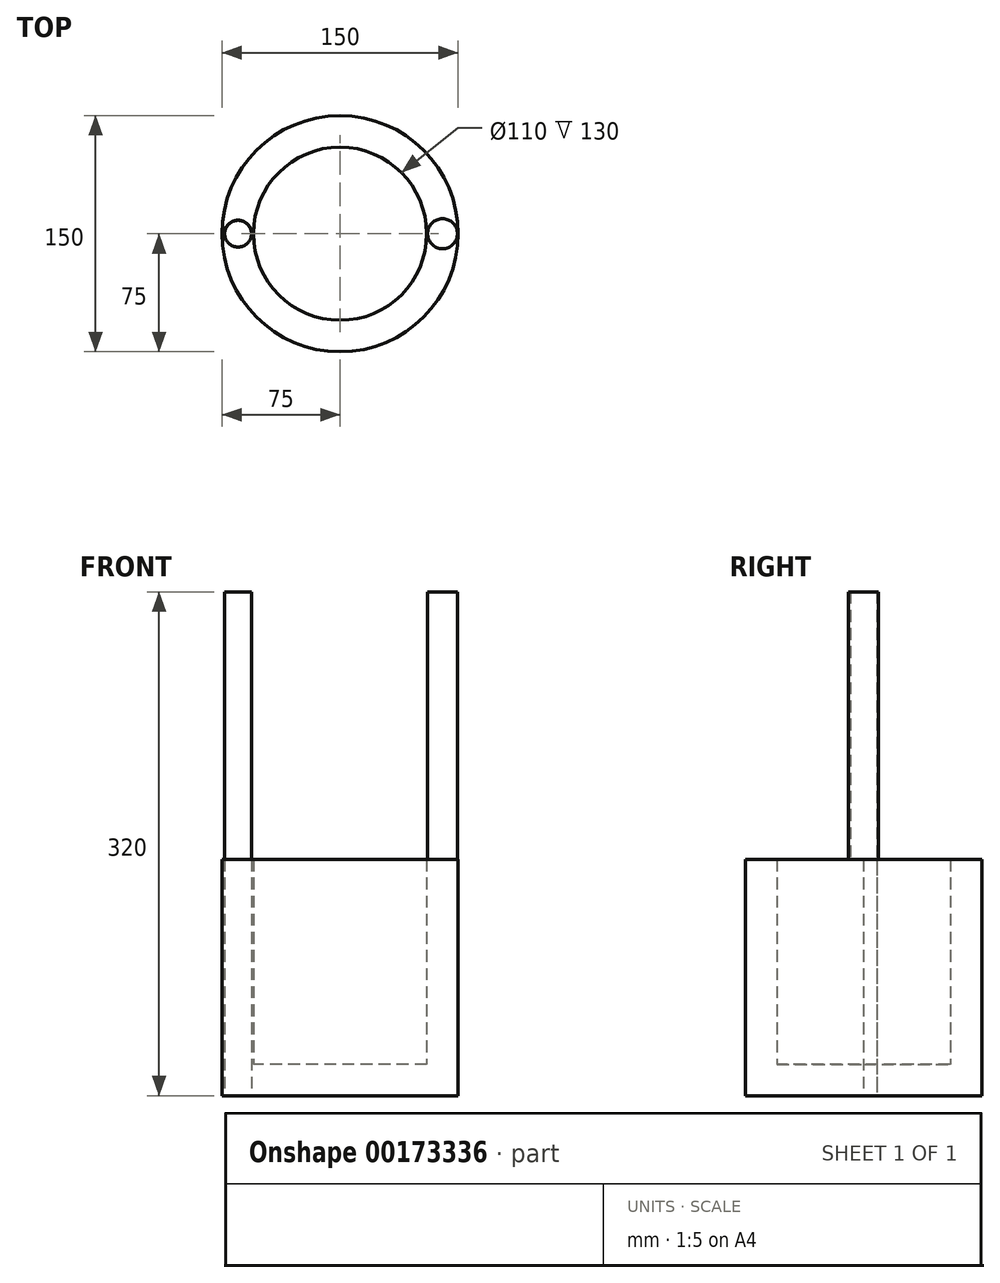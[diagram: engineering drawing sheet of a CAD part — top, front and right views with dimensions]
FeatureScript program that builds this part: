
annotation { "Feature Type Name" : "Feature", "Feature Type Description" : "" }
export const myFeature = defineFeature(function(context is Context, id is Id, definition is map)
    precondition{}
    {
        {
            var Q0;
            Q0=qCreatedBy(makeId("Top.planeOp"),FACE);
            var sketch = newSketch(context, id + "F0", { "sketchPlane" : qUnion([Q0])});
            skCircle(sketch, "E0", {"center": v(0, 0) * mm, "radius": 75 * mm});
            skCircle(sketch, "E1", {"center": v(0, 0) * mm, "radius": 55 * mm});
            skCircle(sketch, "E2", {"center": v(-64.8, 0) * mm, "radius": 8.5 * mm});
            skCircle(sketch, "E3", {"center": v(65.05, 0) * mm, "radius": 9.5 * mm});
            skArc(sketch, "E4", {"start": v(-55, 0) * mm, "mid": v(-65, 10.17) * mm, "end": v(-75, 0) * mm});
            skArc(sketch, "E5", {"start": v(-56.3, 0) * mm, "mid": v(-64.8, 8.57) * mm, "end": v(-73.3, 0) * mm});
            skSolve(sketch);
        }
        {
            var Q0;
            Q0=makeQuery(id+"F0.imprint","IMPRINT",FACE,{"disambiguationData":[TD([[makeQuery(id+"F0.imprint","IMPRINT",EDGE,{"derivedFrom":sQuery(id+"F0.wireOp",EDGE,"E0")}),1.0]])]});
            extrude(context, id + "F1", {"entities" : qUnion([Q0]), "depth" : 150 * mm});
        }
        {
            var Q0;
            Q0=makeQuery(id+"F0.imprint","IMPRINT",FACE,{"disambiguationData":[TD([[makeQuery(id+"F0.imprint","IMPRINT",EDGE,{"derivedFrom":sQuery(id+"F0.wireOp",EDGE,"E0")}),1.0]])]});
            var Q1;
            Q1=makeQuery(id+"F0.imprint","IMPRINT",FACE,{"disambiguationData":[TD([[makeQuery(id+"F0.imprint","IMPRINT",EDGE,{"derivedFrom":sQuery(id+"F0.wireOp",EDGE,"E1")}),1.0]])]});
            extrude(context, id + "F2", {"entities" : qUnion([Q0, Q1]), "operationType" : NewBodyOperationType.ADD, "depth" : 20 * mm});
        }
        {
            var Q0;
            Q0=makeQuery(id+"F0.imprint","IMPRINT",FACE,{"disambiguationData":[TD([[makeQuery(id+"F0.imprint","IMPRINT",EDGE,{"derivedFrom":sQuery(id+"F0.wireOp",EDGE,"E2")}),1.0]])]});
            var Q1;
            Q1=makeQuery(id+"F0.imprint","IMPRINT",FACE,{"disambiguationData":[TD([[makeQuery(id+"F0.imprint","IMPRINT",EDGE,{"derivedFrom":sQuery(id+"F0.wireOp",EDGE,"E3")}),1.0]])]});
            extrude(context, id + "F3", {"entities" : qUnion([Q0, Q1]), "operationType" : NewBodyOperationType.ADD, "depth" : 20 * mm});
        }
        {
            var Q0;
            Q0=makeQuery(id+"F3.opExtrude","CAP_FACE",FACE,{"disambiguationData":[OSD([sQuery(id+"F0.wireOp",EDGE,"E2")])],"isStart":false});
            extrude(context, id + "F4", {"entities" : qUnion([Q0]), "operationType" : NewBodyOperationType.ADD, "depth" : 300 * mm});
        }
        {
            var Q0;
            Q0=makeQuery(id+"F3.opExtrude","CAP_FACE",FACE,{"disambiguationData":[OSD([sQuery(id+"F0.wireOp",EDGE,"E3")])],"isStart":false});
            extrude(context, id + "F5", {"entities" : qUnion([Q0]), "operationType" : NewBodyOperationType.ADD, "depth" : 300 * mm});
        }
    });
